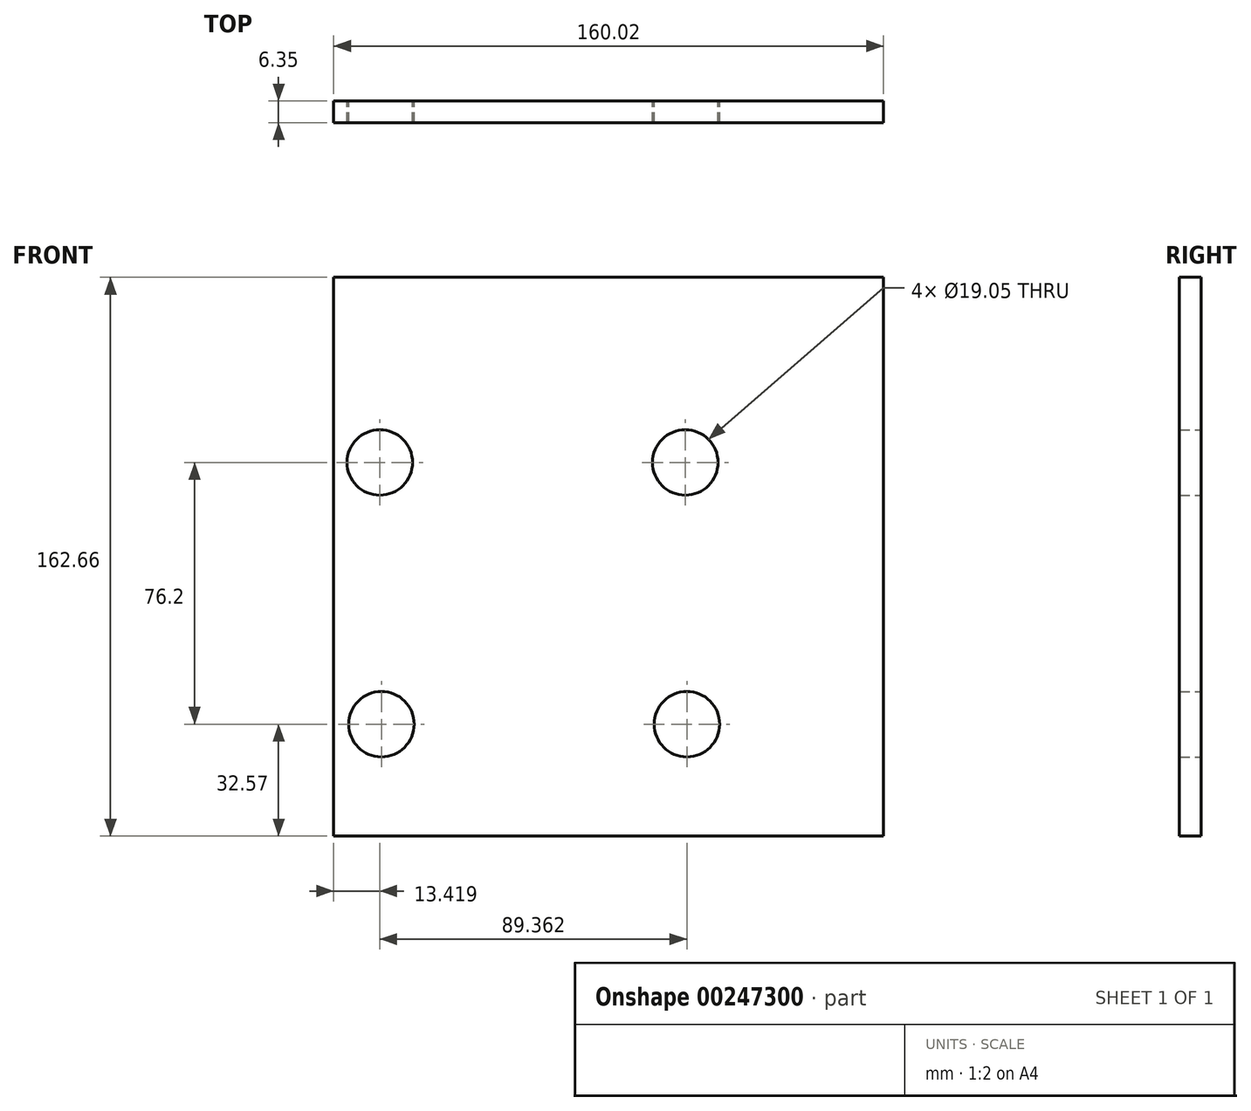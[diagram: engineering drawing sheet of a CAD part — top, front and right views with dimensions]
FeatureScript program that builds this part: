
annotation { "Feature Type Name" : "Feature", "Feature Type Description" : "" }
export const myFeature = defineFeature(function(context is Context, id is Id, definition is map)
    precondition{}
    {
        {
            var Q0;
            Q0=qCreatedBy(makeId("Front.planeOp"),FACE);
            var sketch = newSketch(context, id + "F0", { "sketchPlane" : qUnion([Q0])});
            skLineSegment(sketch, "E0.bottom", {"start": v(-81.4, 92) * mm, "end": v(78.62, 92) * mm});
            skLineSegment(sketch, "E0.top", {"start": v(-81.4, -70.67) * mm, "end": v(78.62, -70.67) * mm});
            skLineSegment(sketch, "E0.left", {"start": v(-81.4, 92) * mm, "end": v(-81.4, -70.67) * mm});
            skLineSegment(sketch, "E0.right", {"start": v(78.62, 92) * mm, "end": v(78.62, -70.67) * mm});
            skCircle(sketch, "E1", {"center": v(-67.98, 38.1) * mm, "radius": 9.53 * mm});
            skCircle(sketch, "E2", {"center": v(20.92, 38.1) * mm, "radius": 9.53 * mm});
            skCircle(sketch, "E3", {"center": v(21.38, -38.1) * mm, "radius": 9.53 * mm});
            skCircle(sketch, "E4", {"center": v(-67.52, -38.1) * mm, "radius": 9.53 * mm});
            skLineSegment(sketch, "E5.bottom", {"start": v(-81.4, 15.24) * mm, "end": v(78.62, 15.24) * mm});
            skLineSegment(sketch, "E5.top", {"start": v(-81.4, -15.24) * mm, "end": v(78.62, -15.24) * mm});
            skLineSegment(sketch, "E5.left", {"start": v(-81.4, 15.24) * mm, "end": v(-81.4, -15.24) * mm});
            skLineSegment(sketch, "E5.right", {"start": v(78.62, 15.24) * mm, "end": v(78.62, -15.24) * mm});
            skLineSegment(sketch, "E6", {"start": v(54.75, 15.24) * mm, "end": v(54.75, -15.24) * mm});
            skSolve(sketch);
        }
        {
            var Q0;
            Q0 = qSketchRegion(id + "F0", true);
            extrude(context, id + "F1", {"entities" : qUnion([Q0]), "depth" : 6.35 * mm});
        }
    });
